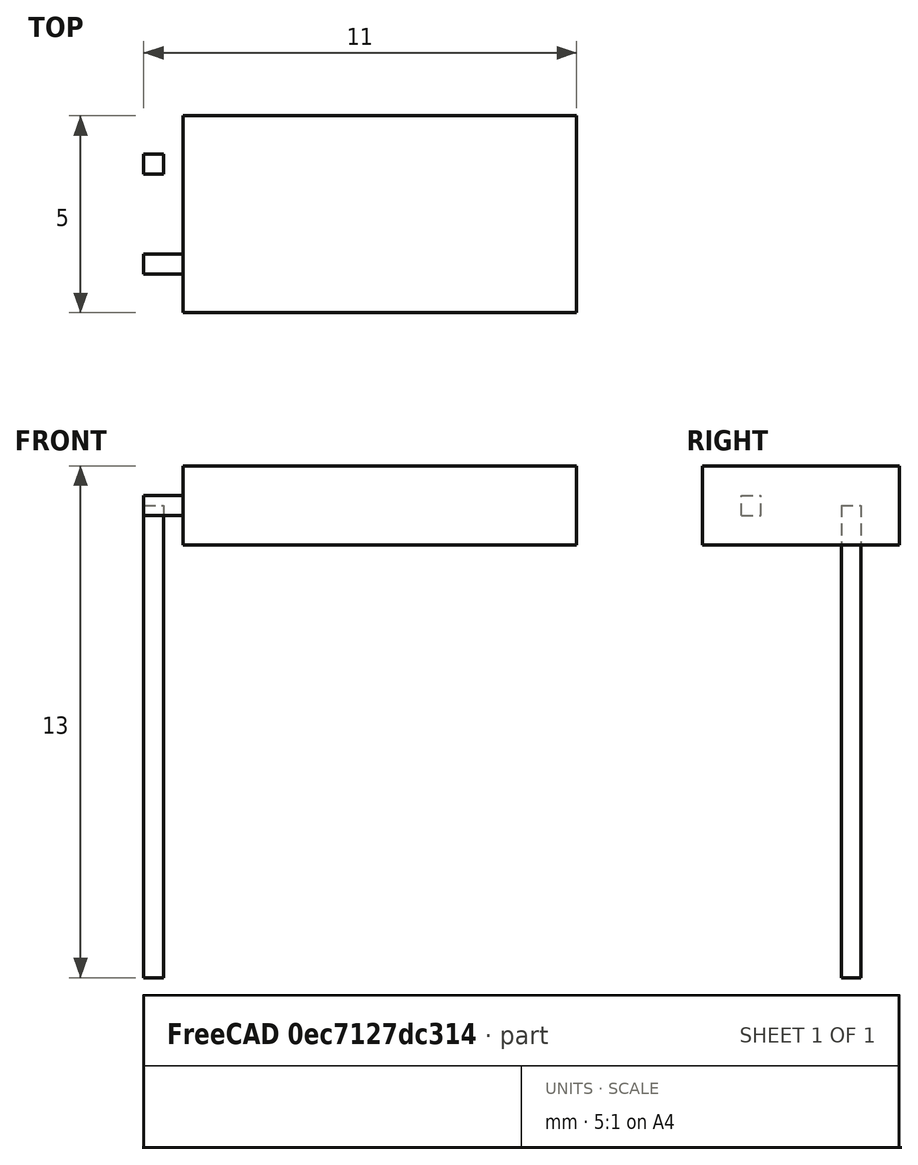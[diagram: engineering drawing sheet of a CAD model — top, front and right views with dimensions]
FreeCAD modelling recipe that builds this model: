
FCSTD DOCUMENT  (FreeCAD 0.16R)
Label: led2
License: All rights reserved
LicenseURL: http://en.wikipedia.org/wiki/All_rights_reserved
objects: Part::Box×3, Part::FeaturePython×2
note: 5 computed .brp shape members not serialized (recipe doc carries the construction recipe); baked Part::Feature solids carry a one-line shape summary decoded from their .brp

FEATURE [Part::Box] Box  label="Cube"
  Height = 2
  Length = 10
  Placement = pos=(-1,0,0) rot=(0,0,1;0rad)
  Width = 5
FEATURE [Part::Box] Box001  label="Cube001"
  Height = 0.5
  Length = 12
  Placement = pos=(-2,0.98,1) rot=(0,1,0;1.5708rad)
  Width = 0.5
FEATURE [Part::FeaturePython] Clone  label="Clone of Cube001"  # Draft clone (typed FeaturePython)
  Objects = -> [Box001]
  Placement = pos=(-2,3.52,1) rot=(0,1,0;1.5708rad)
  Scale = (1,1,1)
FEATURE [Part::Box] Box002  label="Cube002"
  Height = 0.5
  Length = 1
  Placement = pos=(-2,3.52,0.75) rot=(0,0,1;0rad)
  Width = 0.5
FEATURE [Part::FeaturePython] Clone001  label="Clone of Cube002"  # Draft clone (typed FeaturePython)
  Objects = -> [Box002]
  Placement = pos=(-2,0.98,0.75) rot=(0,0,1;0rad)
  Scale = (1,1,1)
